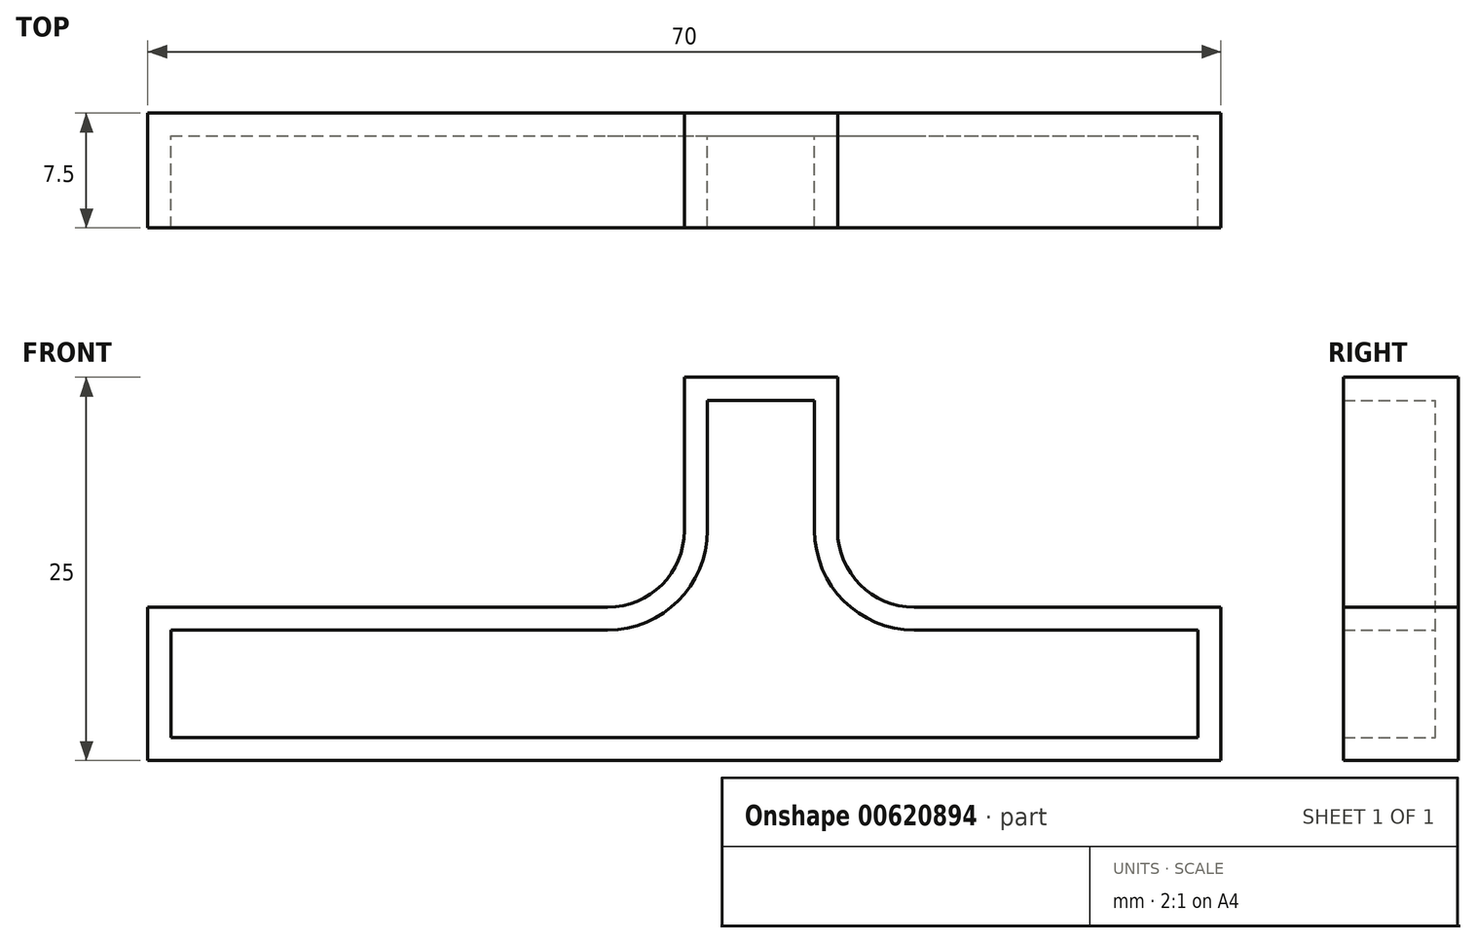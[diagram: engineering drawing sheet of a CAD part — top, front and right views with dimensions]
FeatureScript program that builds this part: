
annotation { "Feature Type Name" : "Feature", "Feature Type Description" : "" }
export const myFeature = defineFeature(function(context is Context, id is Id, definition is map)
    precondition{}
    {
        {
            var Q0;
            Q0=qCreatedBy(makeId("Front.planeOp"),FACE);
            var sketch = newSketch(context, id + "F0", { "sketchPlane" : qUnion([Q0])});
            skLineSegment(sketch, "E0.bottom", {"start": v(0, 0) * mm, "end": v(70, 0) * mm});
            skLineSegment(sketch, "E0.top", {"start": v(0, 10) * mm, "end": v(30, 10) * mm});
            skLineSegment(sketch, "E0.left", {"start": v(0, 0) * mm, "end": v(0, 10) * mm});
            skLineSegment(sketch, "E0.right", {"start": v(70, 0) * mm, "end": v(70, 10) * mm});
            skLineSegment(sketch, "E1.top", {"start": v(35, 25) * mm, "end": v(45, 25) * mm});
            skLineSegment(sketch, "E1.left", {"start": v(35, 15) * mm, "end": v(35, 25) * mm});
            skLineSegment(sketch, "E1.right", {"start": v(45, 15) * mm, "end": v(45, 25) * mm});
            skLineSegment(sketch, "E2.trimOffspring", {"start": v(50, 10) * mm, "end": v(70, 10) * mm});
            skPoint(sketch, "E3.visualSharp", {"position": v(35, 10) * mm});
            skArc(sketch, "E3.filletArc", {"start": v(30, 10) * mm, "mid": v(33.54, 11.46) * mm, "end": v(35, 15) * mm});
            skPoint(sketch, "E4.visualSharp", {"position": v(45, 10) * mm});
            skArc(sketch, "E4.filletArc", {"start": v(45, 15) * mm, "mid": v(46.46, 11.46) * mm, "end": v(50, 10) * mm});
            skSolve(sketch);
        }
        {
            var Q0;
            Q0=qCreatedBy(makeId("Front.planeOp"),FACE);
            var sketch = newSketch(context, id + "F1", { "sketchPlane" : qUnion([Q0])});
            skSolve(sketch);
        }
        {
            var Q0;
            Q0 = qSketchRegion(id + "F1", true);
            var Q1;
            Q1=makeQuery(id+"F0.imprint","IMPRINT",FACE,{"disambiguationData":[TD([[makeQuery(id+"F0.imprint","IMPRINT",EDGE,{"derivedFrom":sQuery(id+"F0.wireOp",EDGE,"E0.bottom")}),1.0]])]});
            extrude(context, id + "F2", {"entities" : qUnion([Q0, Q1]), "depth" : 5 * mm, "offsetDistance" : 25 * mm});
        }
        {
            var Q0;
            Q0 = qSketchRegion(id + "F0", true);
            extrude(context, id + "F3", {"entities" : qUnion([Q0]), "operationType" : NewBodyOperationType.ADD, "endBound" : BoundingType.SYMMETRIC, "depth" : 5 * mm, "offsetDistance" : 25 * mm});
        }
        {
            var Q0;
            Q0=makeQuery(id+"F2.opExtrude","CAP_FACE",FACE,{"disambiguationData":[OSD([sQuery(id+"F0.wireOp",EDGE,"E0.bottom"),sQuery(id+"F0.wireOp",EDGE,"E0.top"),sQuery(id+"F0.wireOp",EDGE,"E0.left"),sQuery(id+"F0.wireOp",EDGE,"E0.right"),sQuery(id+"F0.wireOp",EDGE,"E1.top"),sQuery(id+"F0.wireOp",EDGE,"E1.left"),sQuery(id+"F0.wireOp",EDGE,"E1.right"),sQuery(id+"F0.wireOp",EDGE,"E2.trimOffspring"),sQuery(id+"F0.wireOp",EDGE,"E3.filletArc"),sQuery(id+"F0.wireOp",EDGE,"E4.filletArc")])],"isStart":false});
            shell(context, id + "F4", {"entities" : qUnion([Q0]), "thickness" : 1.5 * mm});
        }
    });
